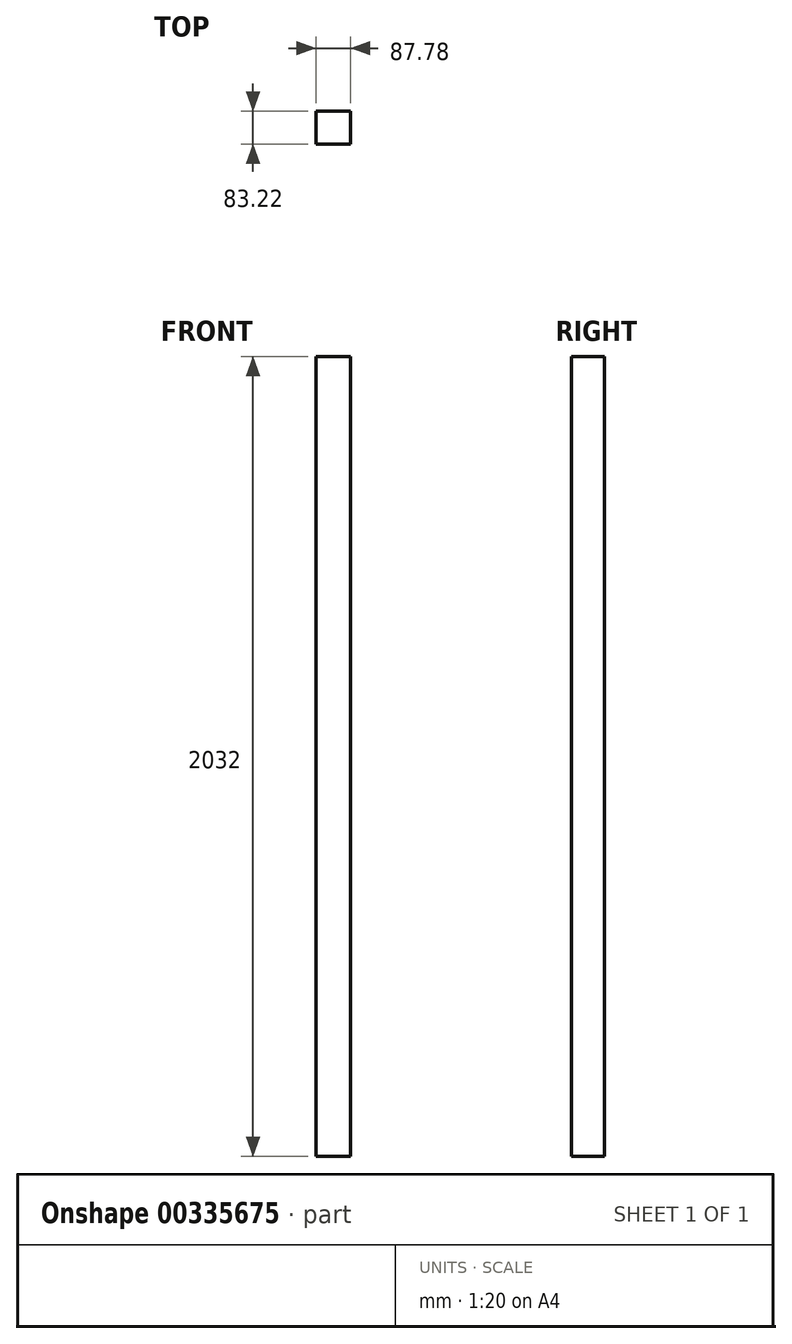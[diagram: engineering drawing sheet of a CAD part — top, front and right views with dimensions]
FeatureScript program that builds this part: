
annotation { "Feature Type Name" : "Feature", "Feature Type Description" : "" }
export const myFeature = defineFeature(function(context is Context, id is Id, definition is map)
    precondition{}
    {
        {
            var Q0;
            Q0=qCreatedBy(makeId("Top.planeOp"),FACE);
            var sketch = newSketch(context, id + "F0", { "sketchPlane" : qUnion([Q0])});
            skLineSegment(sketch, "E0.bottom", {"start": v(-43.9, 41.6) * mm, "end": v(43.9, 41.6) * mm});
            skLineSegment(sketch, "E0.top", {"start": v(-43.9, -41.6) * mm, "end": v(43.9, -41.6) * mm});
            skLineSegment(sketch, "E0.left", {"start": v(-43.9, 41.6) * mm, "end": v(-43.9, -41.6) * mm});
            skLineSegment(sketch, "E0.right", {"start": v(43.9, 41.6) * mm, "end": v(43.9, -41.6) * mm});
            skPoint(sketch, "E0.middle", {"position": v(0, 0) * mm});
            skSolve(sketch);
        }
        {
            var Q0;
            Q0=makeQuery(id+"F0.imprint","IMPRINT",FACE,{"disambiguationData":[TD([[makeQuery(id+"F0.imprint","IMPRINT",EDGE,{"derivedFrom":sQuery(id+"F0.wireOp",EDGE,"E0.bottom")}),-1.0]])]});
            extrude(context, id + "F1", {"entities" : qUnion([Q0]), "endBound" : BoundingType.SYMMETRIC, "depth" : 2032 * mm});
        }
    });
